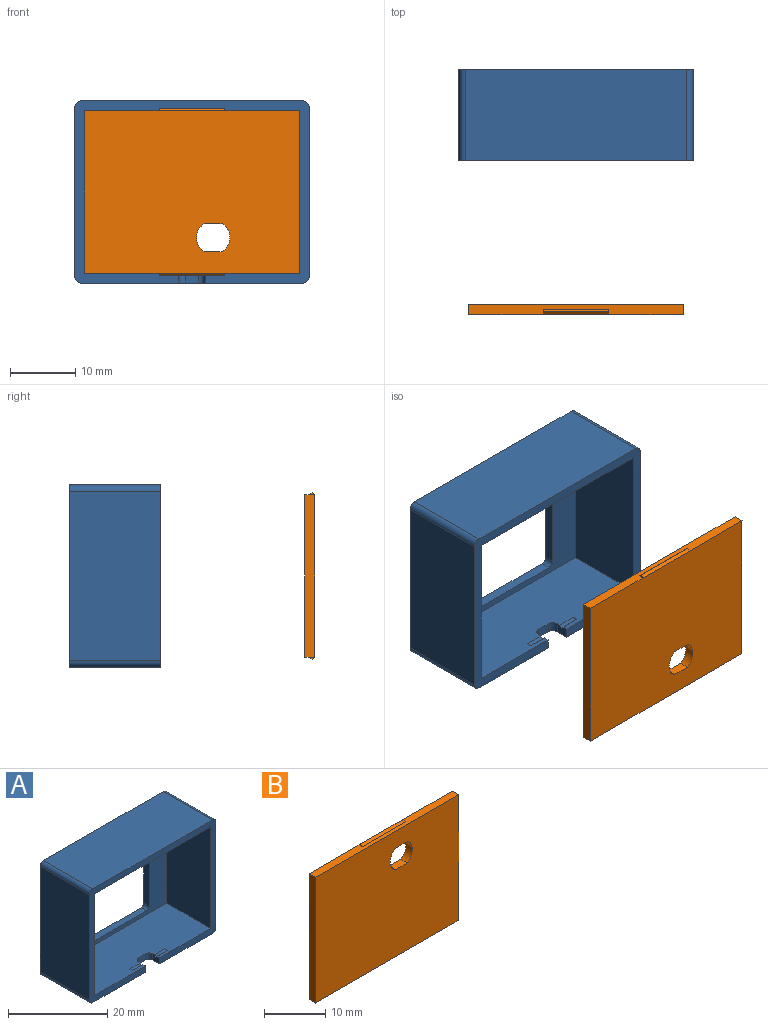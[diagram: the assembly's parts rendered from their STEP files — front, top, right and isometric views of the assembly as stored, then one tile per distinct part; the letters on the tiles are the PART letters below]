
ASSEMBLY  parts=2 mates=1
PART A: 38 faces, bbox 36x14x28 mm
  f0: plane 33x12.5mm, normal (0,0,-1), area 405mm2, adj f5,f8,f9,f16,f34,f35,f36,f37
  f1: plane 21.5x1.5mm, normal (-1,0,0), area 32.2mm2, adj f5,f6,f24,f27
  f2: plane 21.5x1.5mm, normal (0,0,1), area 32.2mm2, adj f5,f6,f24,f25
  f3: plane 21.5x1.5mm, normal (1,0,0), area 32.2mm2, adj f5,f6,f25,f26
  f4: plane 21.5x1.5mm, normal (0,0,-1), area 32.2mm2, adj f5,f6,f26,f27
  f5: plane 33x25mm, normal (0,-1,0), area 296.5mm2, adj f0,f1,f2,f3,f4,f7,f8,f9
  f6: plane 36x28mm, normal (0,1,0), area 478.6mm2, adj f1,f2,f3,f4,f12,f13,f14,f15
  f7: plane 33x12.5mm, normal (0,0,1), area 396.4mm2, adj f5,f8,f9,f10,f11,f16,f17,f18
  f8: plane 25x12.5mm, normal (-1,0,0), area 312.5mm2, adj f0,f5,f7,f16
  f9: plane 25x12.5mm, normal (1,0,0), area 312.5mm2, adj f0,f5,f7,f16
  f10: plane 2x1.5mm, normal (1,0,0), area 2.9mm2, adj f7,f12,f16,f19,f31,f32
  f11: plane 2x1.5mm, normal (-1,0,0), area 2.9mm2, adj f7,f12,f16,f18,f28,f29
  f12: plane 34x14mm, normal (0,0,-1), area 464.4mm2, adj f6,f10,f11,f16,f17,f18,f19,f20
  f13: plane 26x14mm, normal (1,0,0), area 364mm2, adj f6,f16,f20,f21
  f14: plane 34x14mm, normal (0,0,1), area 476mm2, adj f6,f16,f21,f22
  f15: plane 26x14mm, normal (-1,0,0), area 364mm2, adj f6,f16,f22,f23
  f16: plane 36x28mm, normal (0,-1,0), area 176.1mm2, adj f0,f7,f8,f9,f10,f11,f12,f13
  f17: plane 2x1.5mm, normal (0,-1,0), area 3mm2, adj f7,f12,f18,f19
  f18: cylinder r=1mm len=1.5mm, axis (0,0,-1), area 2.4mm2, adj f7,f11,f12,f17
  f19: cylinder r=1mm len=1.5mm, axis (0,0,1), area 2.4mm2, adj f7,f10,f12,f17
  f20: cylinder r=1mm len=14mm, axis (0,-1,0), area 22mm2, adj f6,f12,f13,f16
  f21: cylinder r=1mm len=14mm, axis (0,1,0), area 22mm2, adj f6,f13,f14,f16
  f22: cylinder r=1mm len=14mm, axis (0,-1,0), area 22mm2, adj f6,f14,f15,f16
  f23: cylinder r=1mm len=14mm, axis (0,1,0), area 22mm2, adj f6,f12,f15,f16
  f24: cylinder r=0.75mm len=1.5mm, axis (0,1,0), area 1.8mm2, adj f1,f2,f5,f6
  f25: cylinder r=0.75mm len=1.5mm, axis (0,-1,0), area 1.8mm2, adj f2,f3,f5,f6
  f26: cylinder r=0.75mm len=1.5mm, axis (0,1,0), area 1.8mm2, adj f3,f4,f5,f6
  f27: cylinder r=0.75mm len=1.5mm, axis (0,-1,0), area 1.8mm2, adj f1,f4,f5,f6
  f28: plane 3x0.38mm, normal (0,-0.71,0.71), area 1.6mm2, adj f7,f11,f29,f30
  f29: plane 3x0.38mm, normal (0,0.71,0.71), area 1.6mm2, adj f7,f11,f28,f30
  f30: plane 0.75x0.38mm, normal (-1,0,0), area 0.1mm2, adj f7,f28,f29
  f31: plane 3x0.38mm, normal (0,-0.71,0.71), area 1.6mm2, adj f7,f10,f32,f33
  f32: plane 3x0.38mm, normal (0,0.71,0.71), area 1.6mm2, adj f7,f10,f31,f33
  f33: plane 0.75x0.38mm, normal (1,0,0), area 0.1mm2, adj f7,f31,f32
  f34: plane 0.75x0.38mm, normal (-1,0,0), area 0.1mm2, adj f0,f36,f37
  f35: plane 0.75x0.38mm, normal (1,0,0), area 0.1mm2, adj f0,f36,f37
  f36: plane 10x0.38mm, normal (0,-0.71,-0.71), area 5.3mm2, adj f0,f34,f35,f37
  f37: plane 10x0.38mm, normal (0,0.71,-0.71), area 5.3mm2, adj f0,f34,f35,f36
PART B: 18 faces, bbox 33x1.5x25.8 mm
  f0: plane 33x1.5mm, normal (0,0,-1), area 42mm2, adj f1,f2,f8,f9,f12,f13,f14
  f1: plane 25x1.5mm, normal (-1,0,0), area 37.5mm2, adj f0,f7,f8,f9
  f2: plane 25x1.5mm, normal (1,0,0), area 37.5mm2, adj f0,f7,f8,f9
  f3: cylinder r=2.55mm len=4.3mm, axis (0,1,0), area 7.7mm2, adj f4,f6,f8,f9
  f4: plane 2.74x1.5mm, normal (0,0,1), area 4.1mm2, adj f3,f5,f8,f9
  f5: cylinder r=2.55mm len=4.3mm, axis (0,1,0), area 7.7mm2, adj f4,f6,f8,f9
  f6: plane 2.74x1.5mm, normal (0,0,-1), area 4.1mm2, adj f3,f5,f8,f9
  f7: plane 33x1.5mm, normal (0,0,1), area 42mm2, adj f1,f2,f8,f9,f10,f11,f17
  f8: plane 33x25mm, normal (0,-1,0), area 806.1mm2, adj f0,f1,f2,f3,f4,f5,f6,f7
  f9: plane 33x25mm, normal (0,1,0), area 806.1mm2, adj f0,f1,f2,f3,f4,f5,f6,f7
  f10: plane 0.75x0.38mm, normal (1,0,0), area 0.1mm2, adj f7,f16,f17
  f11: plane 0.75x0.38mm, normal (-1,0,0), area 0.1mm2, adj f7,f16,f17
  f12: plane 0.75x0.38mm, normal (1,0,0), area 0.1mm2, adj f0,f14,f15
  f13: plane 0.75x0.38mm, normal (-1,0,0), area 0.1mm2, adj f0,f14,f15
  f14: plane 10x0.38mm, normal (0,-0.71,-0.71), area 5.3mm2, adj f0,f12,f13,f15
  f15: plane 10x0.38mm, normal (0,0.71,-0.71), area 5.3mm2, adj f9,f12,f13,f14
  f16: plane 10x0.38mm, normal (0,0.71,0.71), area 5.3mm2, adj f9,f10,f11,f17
  f17: plane 10x0.38mm, normal (0,-0.71,0.71), area 5.3mm2, adj f7,f10,f11,f16
PLACE A t=(22.39,1.21,-29.88)mm
PLACE B rot(axis=(-1,0,0),180deg) t=(22.39,-48.95,-29.88)mm
MATE slider B.f9 <-> A.f5  axis (0,-1,0) through (22.39,-36.45,-42.38)mm
